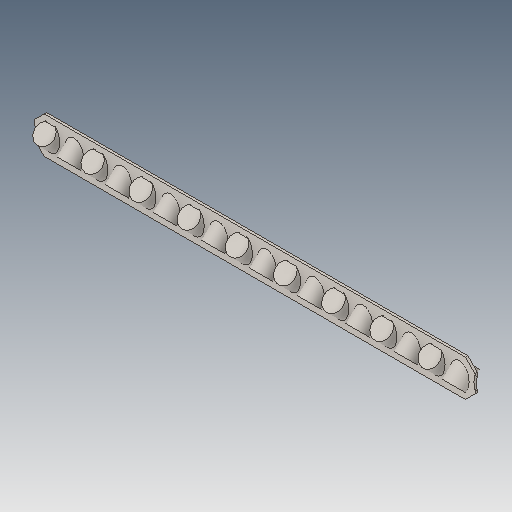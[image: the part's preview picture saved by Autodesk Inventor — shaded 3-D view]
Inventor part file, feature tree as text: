
AUTODESK INVENTOR PART (.ipt)
format: ipt  version: 2019 (Build 230136000, 136)  size: 223,232 bytes
history: native  units: mm
features: other x18, chamfer x1
ambient origin geometry x8: Origin, YZ Plane, XZ Plane, XY Plane, X Axis, Y Axis, Z Axis, Center Point
bodies: Solid1 (feature_tree), Solid2 (feature_tree), Solid3 (feature_tree), Solid4 (feature_tree), Solid5 (feature_tree), Solid6 (feature_tree), Solid7 (feature_tree), Solid8 (feature_tree), Solid9 (feature_tree), Solid10 (feature_tree), Solid11 (feature_tree), Solid12 (feature_tree), Solid13 (feature_tree), Solid14 (feature_tree), Solid15 (feature_tree), Solid16 (feature_tree), Solid17 (feature_tree), Solid18 (feature_tree), Solid19 (feature_tree)
feature tree (19):
  chamfer  "Chamfer1"  [1 undecoded]
  other  "Boss-Extrude3"
  other  "Boss-Extrude4"
  other  "LPattern3[1]"
  other  "LPattern3[2]"
  other  "LPattern3[3]"
  other  "LPattern3[4]"
  other  "LPattern3[10]"
  other  "LPattern3[11]"
  other  "LPattern3[12]"
  other  "LPattern3[13]"
  other  "LPattern3[14]"
  other  "LPattern3[20]"
  other  "LPattern3[21]"
  other  "LPattern3[22]"
  other  "LPattern3[23]"
  other  "LPattern3[29]"
  other  "LPattern3[30]"
  other  "LPattern3[31]"
note: 1 required parameter value undecoded (feature->parameter linkage not recoverable at this tier; creation-order binding heuristic only, values carry confidence <= 0.55)
